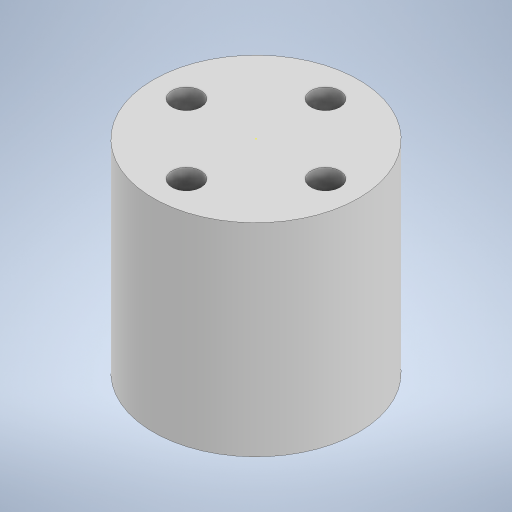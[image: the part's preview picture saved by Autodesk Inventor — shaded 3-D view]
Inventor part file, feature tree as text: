
AUTODESK INVENTOR PART (.ipt)
format: ipt  version: 2024 (Build 280153000, 153)  size: 211,456 bytes
history: native  units: in
note: dims shown in document units (in); Inventor stores cm internally (conversion verified against a paired STEP export)
features: sketch x3, extrude x2
ambient origin geometry x8: Origin, YZ Plane, XZ Plane, XY Plane, X Axis, Y Axis, Z Axis, Center Point
bodies: Solid1 (feature_tree)
feature tree (5):
  extrude  "Extrusion1"  Depth=1.75in TaperAngle=0.0deg
  sketch  "Sketch3"  dims[d6=0.25in d7=0.0in]
  extrude  "Extrusion3"  TaperAngle=0.0deg  [1 undecoded]
  sketch  "Sketch1"  dims[d0=1.772in d1=1.75in d2=0.0in]
  sketch  "Sketch4"  dims[d8=0.6in d9=1.5748in d11=360.0deg d13=1.0in d14=0.0in]
note: 1 required parameter value undecoded (feature->parameter linkage not recoverable at this tier; creation-order binding heuristic only, values carry confidence <= 0.55)
